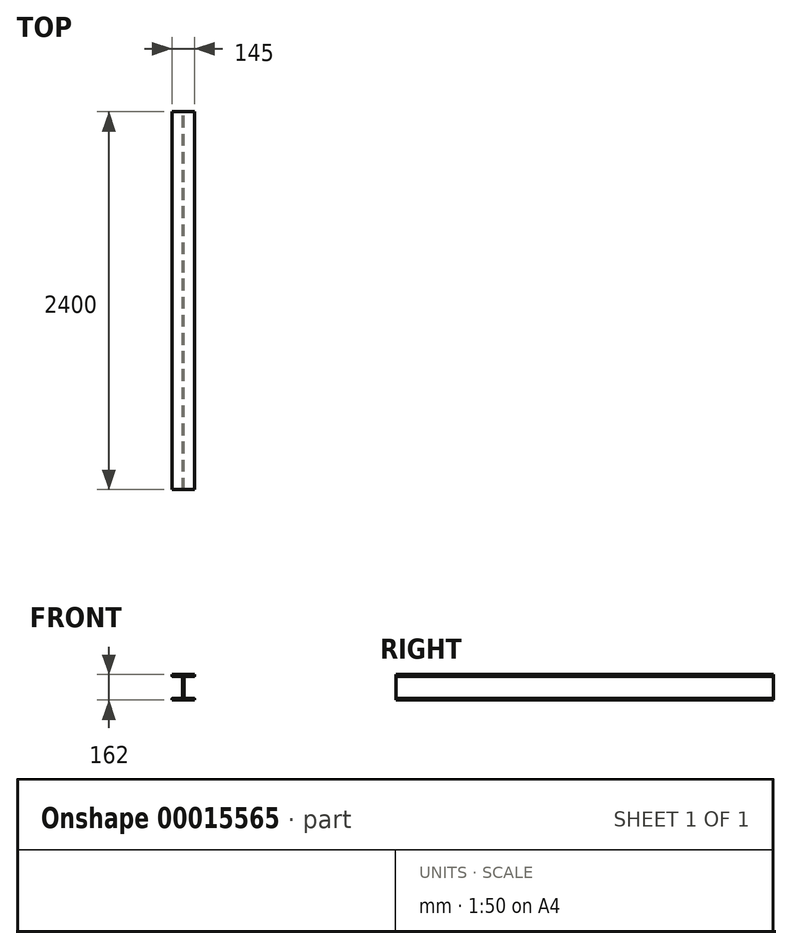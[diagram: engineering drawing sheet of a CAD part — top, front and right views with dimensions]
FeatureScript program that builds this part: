
annotation { "Feature Type Name" : "Feature", "Feature Type Description" : "" }
export const myFeature = defineFeature(function(context is Context, id is Id, definition is map)
    precondition{}
    {
        {
            var Q0;
            Q0=qCreatedBy(makeId("Front.planeOp"),FACE);
            var sketch = newSketch(context, id + "F0", { "sketchPlane" : qUnion([Q0])});
            skLineSegment(sketch, "E0", {"start": v(-72.5, 81) * mm, "end": v(72.5, 81) * mm});
            skLineSegment(sketch, "E1", {"start": v(72.5, 81) * mm, "end": v(72.5, 72.5) * mm});
            skLineSegment(sketch, "E2", {"start": v(69.5, 69.5) * mm, "end": v(12.95, 69.5) * mm});
            skLineSegment(sketch, "E3", {"start": v(4.05, 60.6) * mm, "end": v(4.05, -60.6) * mm});
            skLineSegment(sketch, "E4", {"start": v(12.95, -69.5) * mm, "end": v(69.5, -69.5) * mm});
            skLineSegment(sketch, "E5", {"start": v(72.5, -72.5) * mm, "end": v(72.5, -81) * mm});
            skLineSegment(sketch, "E6", {"start": v(72.5, -81) * mm, "end": v(-72.5, -81) * mm});
            skLineSegment(sketch, "E7", {"start": v(-72.5, -81) * mm, "end": v(-72.5, -72.5) * mm});
            skLineSegment(sketch, "E8", {"start": v(-69.5, -69.5) * mm, "end": v(-12.95, -69.5) * mm});
            skLineSegment(sketch, "E9", {"start": v(-4.05, -60.6) * mm, "end": v(-4.05, 60.6) * mm});
            skLineSegment(sketch, "E10", {"start": v(-12.95, 69.5) * mm, "end": v(-69.5, 69.5) * mm});
            skLineSegment(sketch, "E11", {"start": v(-72.5, 72.5) * mm, "end": v(-72.5, 81) * mm});
            skLineSegment(sketch, "E12", {"start": v(-4.05, 0) * mm, "end": v(4.05, 0) * mm, "construction": true});
            skPoint(sketch, "E13.visualSharp", {"position": v(-4.05, 69.5) * mm});
            skArc(sketch, "E13.filletArc", {"start": v(-4.05, 60.6) * mm, "mid": v(-6.66, 66.9) * mm, "end": v(-12.95, 69.5) * mm});
            skPoint(sketch, "E14.visualSharp", {"position": v(4.05, 69.5) * mm});
            skArc(sketch, "E14.filletArc", {"start": v(12.95, 69.5) * mm, "mid": v(6.66, 66.9) * mm, "end": v(4.05, 60.6) * mm});
            skPoint(sketch, "E15.visualSharp", {"position": v(4.05, -69.5) * mm});
            skArc(sketch, "E15.filletArc", {"start": v(4.05, -60.6) * mm, "mid": v(6.66, -66.9) * mm, "end": v(12.95, -69.5) * mm});
            skPoint(sketch, "E16.visualSharp", {"position": v(-4.05, -69.5) * mm});
            skArc(sketch, "E16.filletArc", {"start": v(-12.95, -69.5) * mm, "mid": v(-6.66, -66.9) * mm, "end": v(-4.05, -60.6) * mm});
            skPoint(sketch, "E17.visualSharp", {"position": v(-72.5, 69.5) * mm});
            skArc(sketch, "E17.filletArc", {"start": v(-72.5, 72.5) * mm, "mid": v(-71.62, 70.38) * mm, "end": v(-69.5, 69.5) * mm});
            skPoint(sketch, "E18.visualSharp", {"position": v(72.5, 69.5) * mm});
            skArc(sketch, "E18.filletArc", {"start": v(69.5, 69.5) * mm, "mid": v(71.62, 70.38) * mm, "end": v(72.5, 72.5) * mm});
            skPoint(sketch, "E19.visualSharp", {"position": v(72.5, -69.5) * mm});
            skArc(sketch, "E19.filletArc", {"start": v(72.5, -72.5) * mm, "mid": v(71.62, -70.38) * mm, "end": v(69.5, -69.5) * mm});
            skPoint(sketch, "E20.visualSharp", {"position": v(-72.5, -69.5) * mm});
            skArc(sketch, "E20.filletArc", {"start": v(-69.5, -69.5) * mm, "mid": v(-71.62, -70.38) * mm, "end": v(-72.5, -72.5) * mm});
            skSolve(sketch);
        }
        {
            var Q0;
            Q0=makeQuery(id+"F0.imprint","IMPRINT",FACE,{"disambiguationData":[TD([[makeQuery(id+"F0.imprint","IMPRINT",EDGE,{"derivedFrom":sQuery(id+"F0.wireOp",EDGE,"E0")}),-1.0]])]});
            extrude(context, id + "F1", {"entities" : qUnion([Q0]), "depth" : 2400 * mm});
        }
    });
